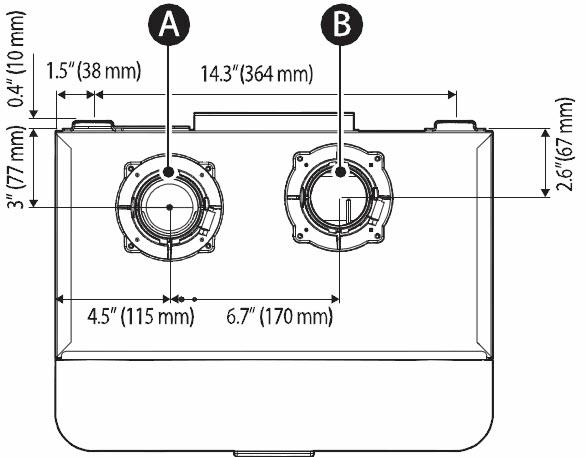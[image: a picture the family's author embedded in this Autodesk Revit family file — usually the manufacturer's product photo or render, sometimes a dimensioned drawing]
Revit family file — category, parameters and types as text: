
# Revit family: Water_Heater-Racks-Navien-NPE-7_Unit_Back_to_Back-02
name_source: partatom
category: Mechanical Equipment
revit_build: Autodesk Revit 2016 (Build: 20150220_1215(x64)
units: mm (PartAtom-declared; Revit-internal decimal feet)

## family parameters
Cut with Voids When Loaded = No
Host = Face
OmniClass Number = 23.65.35.11
OmniClass Title = Supply Water Heaters
Part Type = Normal
Room Calculation Point = No
Round Connector Dimension = Use Diameter
Shared = No

## types (4) — shared parameters
2" Exhaust/Intake = Yes
3" Exhaust/Intake = No
Apparent Load = 0 VA
Assembly Code = D3010500
Certifications = Energy Star | AHRI | CSA | CSA | NFS
Cold Water Inlet = 1"
Configuration = NPE_B7_4B3B
Default Elevation = 48 "
Depth = 23.8 "
Description = 7 Unit Back to Back
Exhaust = 2"
Finish = Metal - Navien - White
Flow Rate = 1 GPM
Flow Rate Note = 35°F (19°C) temp rise: 11.2 GPM (42 L/m) | 45°F (25°C) temp rise: 8.7 GPM (33 L/m) | 67°F (36°C) temp rise: NPE-240A: 5.6 GPM(21 L/m), NPE-240S: 5.7 GPM(22 L/m)
Frequency = 60 Hz
Gas Inlet = 1"
Heating Capacity = 120000.0 Btu/h
Heating Capacity Note = 19,900–199,900 (BTU/H)
Height = 65.5 "
Hot Water Outlet = 1"
Ignition = Electronic ignition
Installation Type = Indoor
Intake = 2"
Keynote = 22 33 00.A1
Manifold(s) = (2) 30019042A
Manufacturer = Navien, Inc.
Manufacturer Fax Number = (949) 420-0430
Natural Gas Manifold Pressure = -0.05" WC to -0.58" WC
Natural Gas Supply Pressure = 3.5"–10.5" WC
Number of Poles = 1
Phase = 1
Power Factor = 1
Product Documentation Link = https://www.navieninc.com
Product Name = NPE Series Tankless Water Heaters w/ Racks
Product Page URL = https://www.navieninc.com
Propane Gas Manifold Pressure = -0.10" WC to -0.78" WC
Propane Gas Supply Pressure = 8"–13" WC
Rack(s) = (1) GFFM-KDIZUS-003 + (3) GFFM-KDIZUS-004
Required Cascade Operation Accessory = (7) 30014367A (Common Vent Damper & Cascade Communication Cable) or (6) GXXX000546 (Individual Vent Cascade Communication Cable)
URL = https://www.navieninc.com
Venting = Exhaust: 2" PVC, CPVC, PP, SS / 2" special gas vent type BH (Class II, A/B/C) | Intake: 2" PVC, CPVC, PP, SS / 2" special gas vent type BH (Class II, A/B/C) | Vent clearances: 0" to combustibles
Venting Type = Forced draft direct vent
Version = 2016 - v1.0.a
Voltage = 120 V
Water Pressure = 15–150 PSI
Wi-Fi Ready = NaviLink Wi-Fi Control: PBCM-AS-001
Width = 82.3 "

## per-type parameters (varying)
| type | Constraints | Model | Natural Gas | Propane Gas | Recirculation Inlet | Recirculation Inlet Visibility | Tankless Water Heaters | Weight |
| Natural Gas - Recirculating System - NPE-240A(Advanced)-NG | 6 | (7) NPE-240A-NG | Yes | No | 0" | Yes | (7) NPE-240A-NG | 82.00 lbf |
| Natural Gas - NPE-240S(Standard)-NG | 7 | (7) NPE-240S-NG | Yes | No | 1" | No | (7) NPE-240S-NG | 75.00 lbf |
| Propane Gas - Recirculating System - NPE-240A(Advanced)-LPG | 6 | (7) NPE-240A-LPG | No | Yes | 0" | Yes | (7) NPE-240A-LPG | 82.00 lbf |
| Propane Gas - NPE-240S(Standard)-LPG | 7 | (7) NPE-240S-LPG | No | Yes | 1" | No | (7) NPE-240S-LPG | 75.00 lbf |

## geometry (parser evidence)
native form markers: Sweep x18
no freeform markers — native parametric forms only
